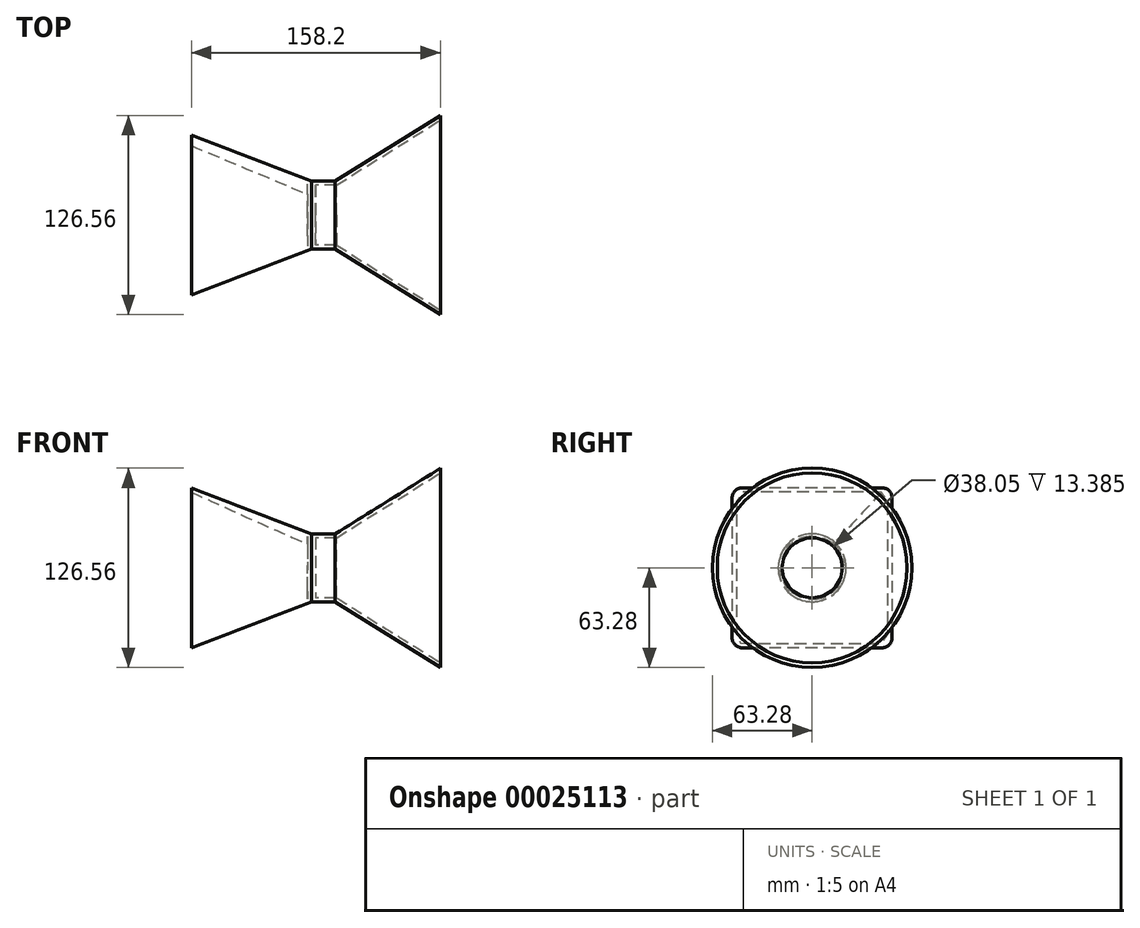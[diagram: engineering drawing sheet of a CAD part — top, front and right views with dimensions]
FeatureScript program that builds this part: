
annotation { "Feature Type Name" : "Feature", "Feature Type Description" : "" }
export const myFeature = defineFeature(function(context is Context, id is Id, definition is map)
    precondition{}
    {
        {
            var Q0;
            Q0=qCreatedBy(makeId("Top.planeOp"),FACE);
            var sketch = newSketch(context, id + "F0", { "sketchPlane" : qUnion([Q0])});
            skLineSegment(sketch, "E0", {"start": v(0, 0) * mm, "end": v(82, 0) * mm});
            skLineSegment(sketch, "E1.2", {"start": v(0, 21.57) * mm, "end": v(15.2, 21.57) * mm});
            skLineSegment(sketch, "E1.3", {"start": v(15.2, 21.57) * mm, "end": v(82, 63.28) * mm});
            skLineSegment(sketch, "E2", {"start": v(0, 0) * mm, "end": v(0, 21.57) * mm});
            skPoint(sketch, "E3.orphan", {"position": v(-2.54, -2.54) * mm});
            skPoint(sketch, "E4.orphan", {"position": v(-2.54, 21.57) * mm});
            skPoint(sketch, "E5.orphan", {"position": v(0, -2.54) * mm});
            skLineSegment(sketch, "E6", {"start": v(82, 0) * mm, "end": v(82, 63.28) * mm});
            skPoint(sketch, "E7.orphan", {"position": v(79.46, 0) * mm});
            skSolve(sketch);
        }
        {
            var Q0;
            {var subQ2=sQuery(id+"F0.wireOp",EDGE,"cc1a8448-8d2b-47d4-b66e-bdffe652290d");Q0=makeQuery(id+"F0.imprint","IMPRINT",FACE,{"disambiguationData":[TD([[makeQuery(id+"F0.imprint","IMPRINT",EDGE,{"derivedFrom":subQ2}),1.0]])]});}
            var Q1;
            Q1=makeQuery(id+"F0.imprint","IMPRINT",FACE,{"disambiguationData":[TD([[makeQuery(id+"F0.imprint","IMPRINT",EDGE,{"derivedFrom":sQuery(id+"F0.wireOp",EDGE,"E0")}),1.0]])]});
            var Q2;
            Q2=sQuery(id+"F0.wireOp",EDGE,"E0");
            revolve(context, id + "F1", {"entities" : qUnion([Q0, Q1]), "axis" : qUnion([Q2]), "revolveType" : RevolveType.FULL});
        }
        {
            var Q0;
            Q0=makeQuery(id+"F1.opRevolve","SWEPT_FACE",FACE,{"disambiguationData":[OSD([sQuery(id+"F0.wireOp",EDGE,"E2")])]});
            cPlane(context, id + "F2", {"entities" : qUnion([Q0]), "cplaneType" : CPlaneType.OFFSET, "offset" : 76.2 * mm, "width" : 152.4 * mm, "height" : 152.4 * mm});
        }
        {
            var Q0;
            Q0=qCreatedBy(id+"F2.planeOp",FACE);
            var sketch = newSketch(context, id + "F3", { "sketchPlane" : qUnion([Q0])});
            skLineSegment(sketch, "E8.bottom", {"start": v(-44.45, 50.8) * mm, "end": v(44.45, 50.8) * mm});
            skLineSegment(sketch, "E8.top", {"start": v(-44.45, -50.8) * mm, "end": v(44.45, -50.8) * mm});
            skLineSegment(sketch, "E8.left", {"start": v(-50.8, 44.45) * mm, "end": v(-50.8, -44.45) * mm});
            skLineSegment(sketch, "E8.right", {"start": v(50.8, 44.45) * mm, "end": v(50.8, -44.45) * mm});
            skPoint(sketch, "E9.visualSharp", {"position": v(50.8, 50.8) * mm});
            skArc(sketch, "E9.filletArc", {"start": v(50.8, 44.45) * mm, "mid": v(48.94, 48.94) * mm, "end": v(44.45, 50.8) * mm});
            skPoint(sketch, "E10.visualSharp", {"position": v(50.8, -50.8) * mm});
            skArc(sketch, "E10.filletArc", {"start": v(44.45, -50.8) * mm, "mid": v(48.94, -48.94) * mm, "end": v(50.8, -44.45) * mm});
            skPoint(sketch, "E11.visualSharp", {"position": v(-50.8, -50.8) * mm});
            skArc(sketch, "E11.filletArc", {"start": v(-50.8, -44.45) * mm, "mid": v(-48.94, -48.94) * mm, "end": v(-44.45, -50.8) * mm});
            skPoint(sketch, "E12.visualSharp", {"position": v(-50.8, 50.8) * mm});
            skArc(sketch, "E12.filletArc", {"start": v(-44.45, 50.8) * mm, "mid": v(-48.94, 48.94) * mm, "end": v(-50.8, 44.45) * mm});
            skLineSegment(sketch, "E13.0", {"start": v(-44.45, 53.34) * mm, "end": v(44.45, 53.34) * mm});
            skSolve(sketch);
        }
        {
            var Q0;
            Q0=makeQuery(id+"F3.imprint","IMPRINT",FACE,{"disambiguationData":[TD([[makeQuery(id+"F3.imprint","IMPRINT",EDGE,{"derivedFrom":sQuery(id+"F3.wireOp",EDGE,"E8.bottom")}),-1.0]])]});
            var Q1;
            Q1=makeQuery(id+"F1.opRevolve","SWEPT_FACE",FACE,{"disambiguationData":[OSD([sQuery(id+"F0.wireOp",EDGE,"E2")])]});
            loft(context, id + "F4", {"sheetProfilesArray" : [{ "sheetProfileEntities" : qUnion([Q0]) }, { "sheetProfileEntities" : qUnion([Q1]) }]});
        }
        {
            var Q0;
            Q0=makeQuery(id+"F4.opLoft","CAP_FACE",FACE,{"disambiguationData":[OSD([makeQuery(id+"F3.imprint","IMPRINT",FACE,{"disambiguationData":[TD([[makeQuery(id+"F3.imprint","IMPRINT",EDGE,{"derivedFrom":sQuery(id+"F3.wireOp",EDGE,"E8.bottom")}),-1.0]])]})])],"isStart":true});
            shell(context, id + "F5", {"entities" : qUnion([Q0]), "thickness" : 2.54 * mm});
        }
        {
            var Q0;
            Q0=makeQuery(id+"F1.opRevolve","SWEPT_FACE",FACE,{"disambiguationData":[OSD([sQuery(id+"F0.wireOp",EDGE,"E6")])]});
            shell(context, id + "F6", {"entities" : qUnion([Q0]), "thickness" : 2.54 * mm});
        }
    });
